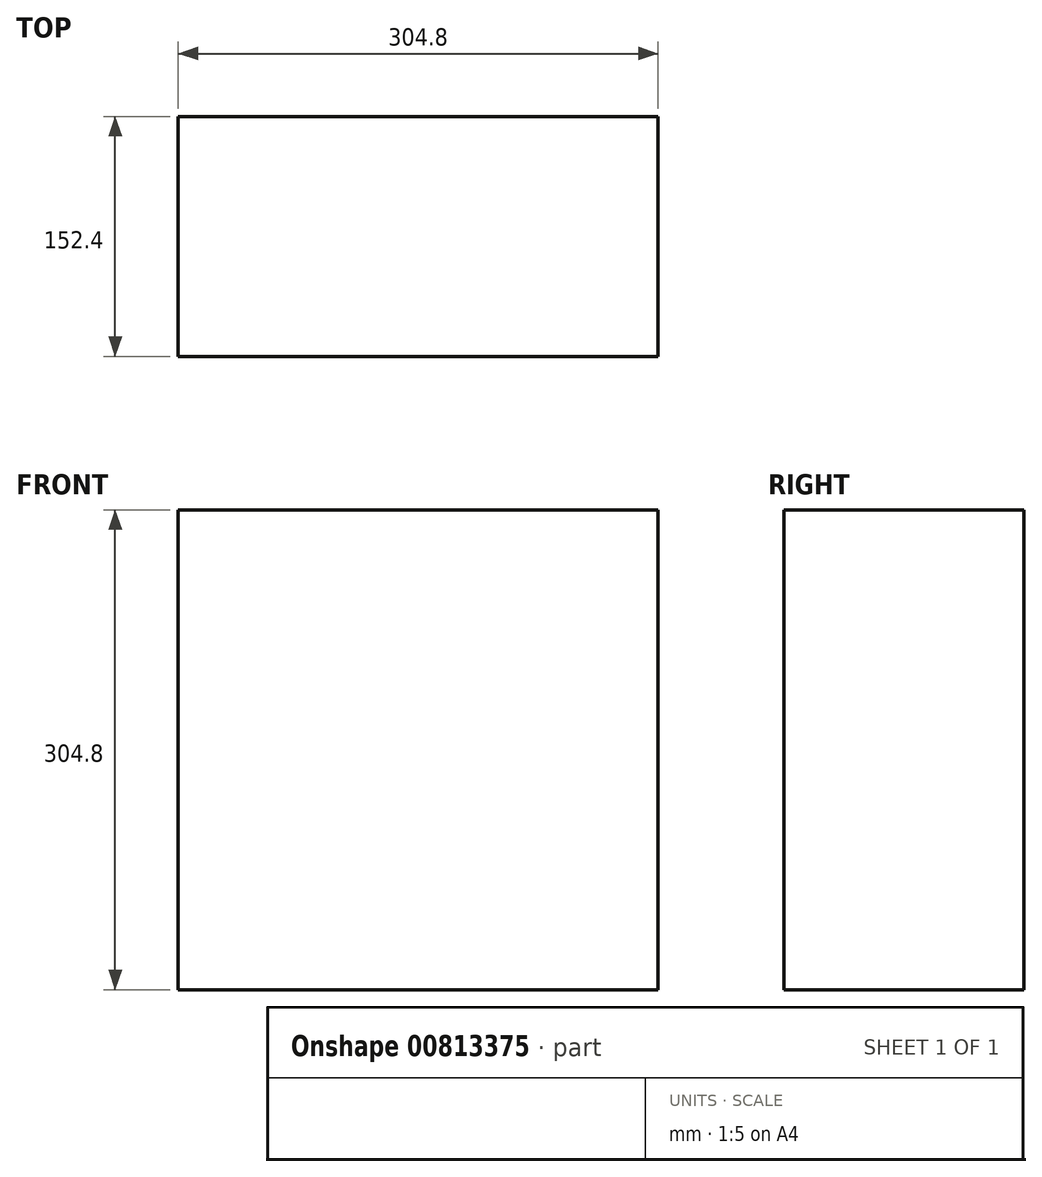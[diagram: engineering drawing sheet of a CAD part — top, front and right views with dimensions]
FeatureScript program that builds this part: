
annotation { "Feature Type Name" : "Feature", "Feature Type Description" : "" }
export const myFeature = defineFeature(function(context is Context, id is Id, definition is map)
    precondition{}
    {
        {
            var Q0;
            Q0=qCreatedBy(makeId("Front.planeOp"),FACE);
            var sketch = newSketch(context, id + "F0", { "sketchPlane" : qUnion([Q0])});
            skLineSegment(sketch, "E0.bottom", {"start": v(-169.66, 206.11) * mm, "end": v(135.14, 206.11) * mm});
            skLineSegment(sketch, "E0.top", {"start": v(-169.66, -98.69) * mm, "end": v(135.14, -98.69) * mm});
            skLineSegment(sketch, "E0.left", {"start": v(-169.66, 206.11) * mm, "end": v(-169.66, -98.69) * mm});
            skLineSegment(sketch, "E0.right", {"start": v(135.14, 206.11) * mm, "end": v(135.14, -98.69) * mm});
            skSolve(sketch);
        }
        {
            var Q0;
            Q0=makeQuery(id+"F0.imprint","IMPRINT",FACE,{"disambiguationData":[TD([[makeQuery(id+"F0.imprint","IMPRINT",EDGE,{"derivedFrom":sQuery(id+"F0.wireOp",EDGE,"E0.bottom")}),-1.0]])]});
            extrude(context, id + "F1", {"entities" : qUnion([Q0]), "depth" : 152.4 * mm, "offsetDistance" : 25.4 * mm});
        }
    });
